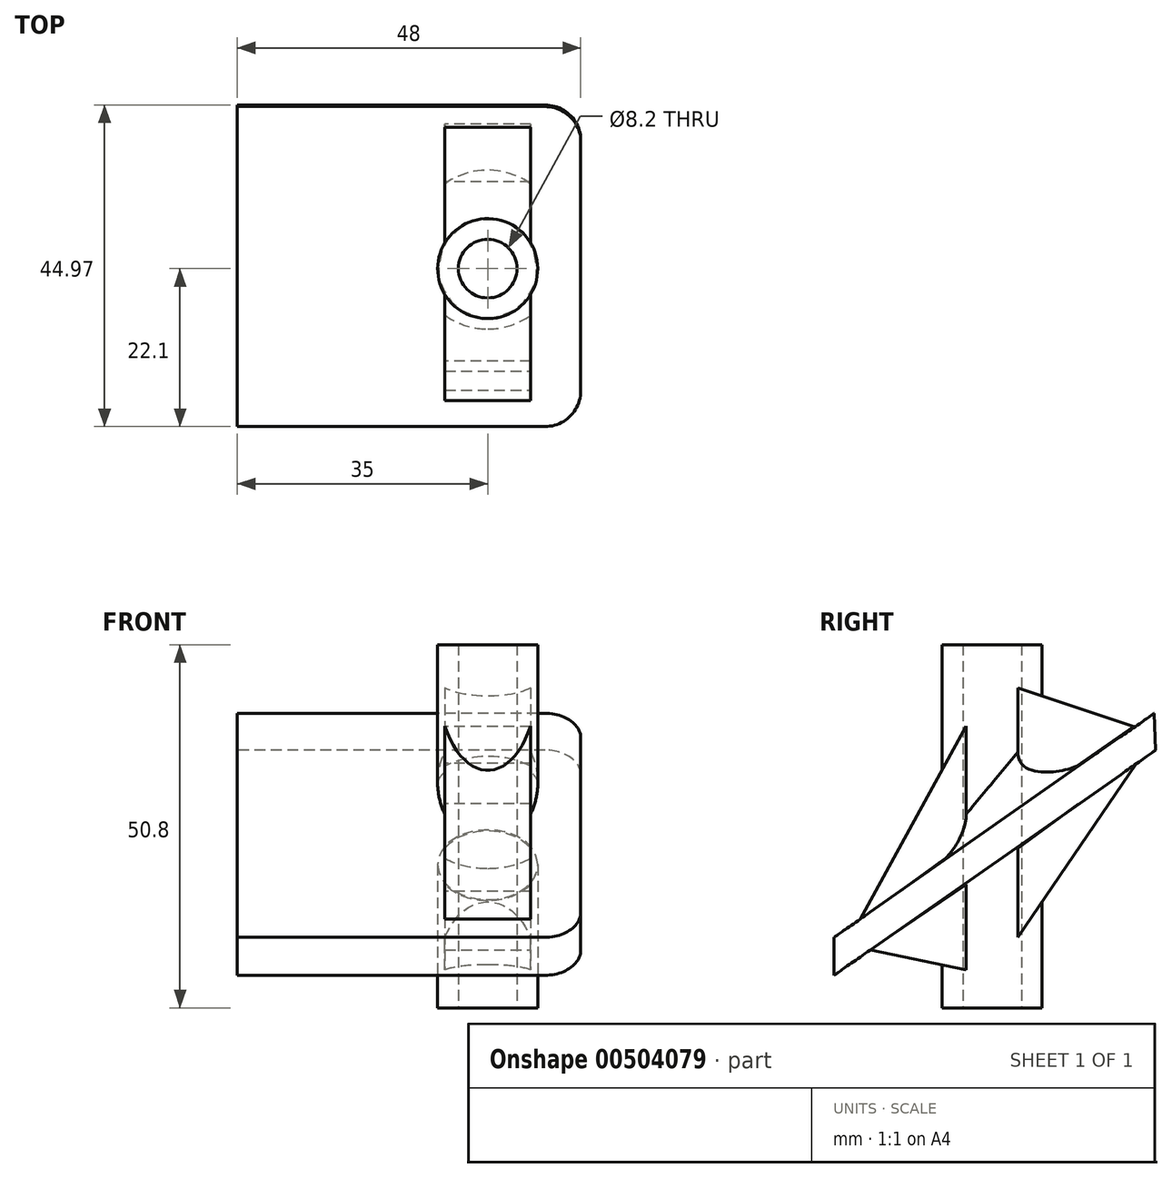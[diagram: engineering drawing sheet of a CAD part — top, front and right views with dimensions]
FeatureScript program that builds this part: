
annotation { "Feature Type Name" : "Feature", "Feature Type Description" : "" }
export const myFeature = defineFeature(function(context is Context, id is Id, definition is map)
    precondition{}
    {
        {
            var Q0;
            Q0=qCreatedBy(makeId("Top.planeOp"),FACE);
            var sketch = newSketch(context, id + "F0", { "sketchPlane" : qUnion([Q0])});
            skCircle(sketch, "E0", {"center": v(0, 0) * mm, "radius": 4.1 * mm});
            skCircle(sketch, "E1", {"center": v(0, 0) * mm, "radius": 7 * mm});
            skSolve(sketch);
        }
        {
            var Q0;
            Q0=makeQuery(id+"F0.imprint","IMPRINT",FACE,{"disambiguationData":[TD([[makeQuery(id+"F0.imprint","IMPRINT",EDGE,{"derivedFrom":sQuery(id+"F0.wireOp",EDGE,"E0")}),-1.0]])]});
            extrude(context, id + "F1", {"entities" : qUnion([Q0]), "depth" : 50.8 * mm});
        }
        {
            var Q0;
            Q0=qCreatedBy(makeId("Right.planeOp"),FACE);
            var sketch = newSketch(context, id + "F2", { "sketchPlane" : qUnion([Q0])});
            skLineSegment(sketch, "E2", {"start": v(22.66, 41.2) * mm, "end": v(-44.84, 41.2) * mm});
            skLineSegment(sketch, "E3", {"start": v(0, 0) * mm, "end": v(0, 67.72) * mm});
            skPoint(sketch, "E4", {"position": v(-29.87, 41.2) * mm});
            skLineSegment(sketch, "E5", {"start": v(0, 25.33) * mm, "end": v(22.66, 41.2) * mm});
            skLineSegment(sketch, "E6", {"start": v(0, 25.33) * mm, "end": v(-38.64, -1.73) * mm});
            skPoint(sketch, "E7", {"position": v(0, 50.77) * mm});
            skLineSegment(sketch, "E8", {"start": v(-22.1, 4.56) * mm, "end": v(22.87, 36.05) * mm});
            skLineSegment(sketch, "E9", {"start": v(-22.1, 4.56) * mm, "end": v(-22.1, 9.86) * mm});
            skLineSegment(sketch, "E10", {"start": v(22.66, 41.2) * mm, "end": v(22.87, 36.05) * mm});
            skSolve(sketch);
        }
        {
            var Q0;
            Q0=qCreatedBy(makeId("Right.planeOp"),FACE);
            var sketch = newSketch(context, id + "F3", { "sketchPlane" : qUnion([Q0])});
            skPoint(sketch, "E11", {"position": v(20.48, 34.59) * mm});
            skPoint(sketch, "E12", {"position": v(0, 4.58) * mm});
            skPoint(sketch, "E13", {"position": v(0, 19.72) * mm});
            skLineSegment(sketch, "E14", {"start": v(20.48, 34.59) * mm, "end": v(0, 4.58) * mm});
            skLineSegment(sketch, "E15", {"start": v(20.48, 34.59) * mm, "end": v(0, 19.72) * mm});
            skPoint(sketch, "E16", {"position": v(0, 25.6) * mm});
            skPoint(sketch, "E17", {"position": v(19.77, 39.32) * mm});
            skLineSegment(sketch, "E18", {"start": v(0, 25.6) * mm, "end": v(-18.54, 12.23) * mm});
            skLineSegment(sketch, "E19", {"start": v(19.77, 39.32) * mm, "end": v(0, 25.6) * mm});
            skPoint(sketch, "E20", {"position": v(0, 45.94) * mm});
            skLineSegment(sketch, "E21", {"start": v(0, 45.94) * mm, "end": v(-18.54, 12.23) * mm});
            skLineSegment(sketch, "E22", {"start": v(0, 45.94) * mm, "end": v(19.77, 39.32) * mm});
            skPoint(sketch, "E23", {"position": v(-17.08, 8.13) * mm});
            skLineSegment(sketch, "E24", {"start": v(0, 4.58) * mm, "end": v(-17.08, 8.13) * mm});
            skLineSegment(sketch, "E25", {"start": v(0, 19.72) * mm, "end": v(-17.08, 8.13) * mm});
            skSolve(sketch);
        }
        {
            var Q0;
            {var subQ5=sQuery(id+"F2.wireOp",EDGE,"ZiOkMTBJ-UBI1-K0Fz-GPcT-TLhmjK109Hpe");Q0=makeQuery(id+"F2.imprint","IMPRINT",FACE,{"disambiguationData":[TD([[makeQuery(id+"F2.imprint","IMPRINT",EDGE,{"derivedFrom":subQ5}),-1.0]])]});}
            var Q1;
            {var subQ0=sQuery(id+"F2.wireOp",EDGE,"E5");Q1=makeQuery(id+"F2.imprint","IMPRINT",FACE,{"disambiguationData":[TD([[makeQuery(id+"F2.imprint","IMPRINT",EDGE,{"derivedFrom":subQ0}),-1.0]])]});}
            var Q2;
            {var subQ5=sQuery(id+"F2.wireOp",EDGE,"E9");Q2=makeQuery(id+"F2.imprint","IMPRINT",FACE,{"disambiguationData":[TD([[makeQuery(id+"F2.imprint","IMPRINT",EDGE,{"derivedFrom":subQ5}),-1.0]])]});}
            extrude(context, id + "F4", {"entities" : qUnion([Q0, Q1, Q2]), "operationType" : NewBodyOperationType.ADD, "depth" : 13 * mm, "hasSecondDirection" : true, "secondDirectionOppositeDirection" : true, "secondDirectionDepth" : 35 * mm});
        }
        {
            var Q0;
            Q0=makeQuery(id+"F3.imprint","IMPRINT",FACE,{"disambiguationData":[TD([[makeQuery(id+"F3.imprint","IMPRINT",EDGE,{"derivedFrom":sQuery(id+"F3.wireOp",EDGE,"E14")}),-1.0]])]});
            var Q1;
            Q1=makeQuery(id+"F3.imprint","IMPRINT",FACE,{"disambiguationData":[TD([[makeQuery(id+"F3.imprint","IMPRINT",EDGE,{"derivedFrom":sQuery(id+"F3.wireOp",EDGE,"E18")}),-1.0]])]});
            extrude(context, id + "F5", {"entities" : qUnion([Q0, Q1]), "operationType" : NewBodyOperationType.ADD, "endBound" : BoundingType.SYMMETRIC, "depth" : 12 * mm});
        }
        {
            var Q0;
            Q0=makeQuery(id+"F4.boolean.opBoolean","INTERSECT",EDGE,{"derivedFrom":[makeQuery(id+"F1.opExtrude","SWEPT_FACE",FACE,{"disambiguationData":[OSD([sQuery(id+"F0.wireOp",EDGE,"E1")])]}),makeQuery(id+"F4.opExtrude","SWEPT_FACE",FACE,{"disambiguationData":[OSD([sQuery(id+"F2.wireOp",EDGE,"E5"),sQuery(id+"F2.wireOp",EDGE,"E6")])]})]});
            fillet(context, id + "F6", {"entities" : qUnion([Q0]), "radius" : 5 * mm, "tangentPropagation" : true, "allowEdgeOverflow" : false});
        }
        {
            var Q0;
            Q0=makeQuery(id+"F4.opExtrude","CAP_EDGE",EDGE,{"disambiguationData":[OSD([sQuery(id+"F2.wireOp",EDGE,"E9")])],"isStart":false});
            var Q1;
            Q1=makeQuery(id+"F4.opExtrude","CAP_EDGE",EDGE,{"disambiguationData":[OSD([sQuery(id+"F2.wireOp",EDGE,"E10")])],"isStart":false});
            fillet(context, id + "F7", {"entities" : qUnion([Q0, Q1]), "radius" : 5 * mm, "tangentPropagation" : true, "allowEdgeOverflow" : false});
        }
        {
            var Q0;
            Q0=makeQuery(id+"F0.imprint","IMPRINT",FACE,{"disambiguationData":[TD([[makeQuery(id+"F0.imprint","IMPRINT",EDGE,{"derivedFrom":sQuery(id+"F0.wireOp",EDGE,"E0")}),1.0]])]});
            extrude(context, id + "F8", {"entities" : qUnion([Q0]), "operationType" : NewBodyOperationType.REMOVE, "depth" : 55.4 * mm});
        }
    });
